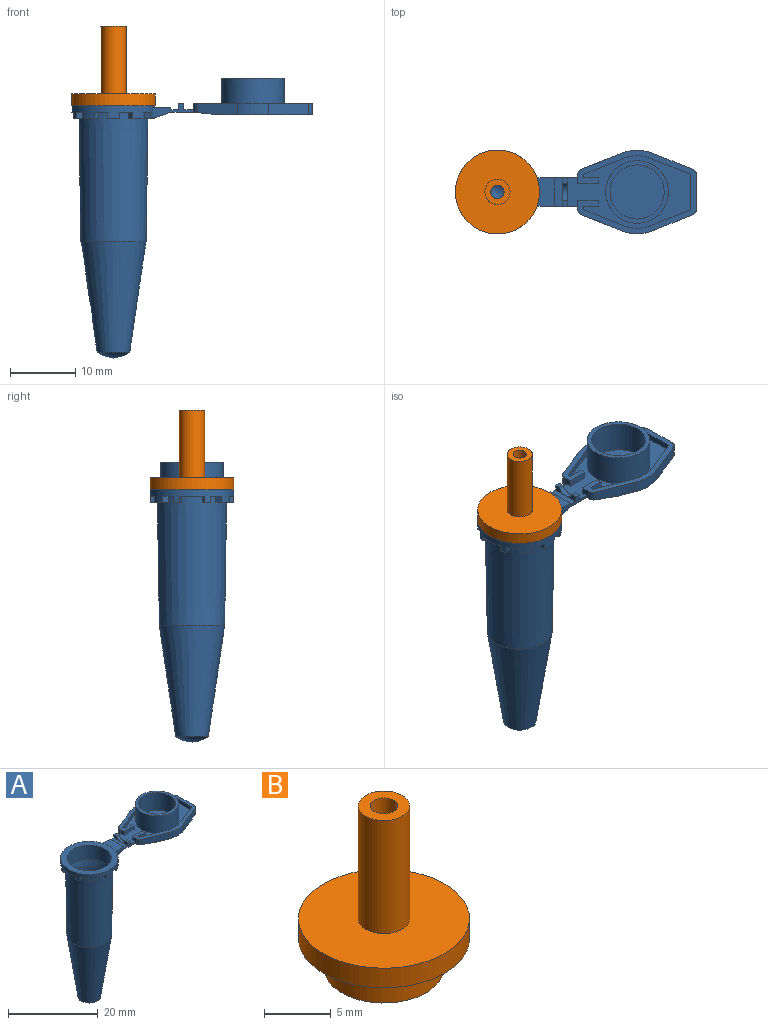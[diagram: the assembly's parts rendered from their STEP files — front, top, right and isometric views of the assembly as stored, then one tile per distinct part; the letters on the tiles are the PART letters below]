
ASSEMBLY  parts=2 mates=1
PART A: 116 faces, bbox 36.9x12.8x42.8 mm
  f0: plane 18.87x11.1mm, normal (0,0,1), area 74.1mm2, adj f1,f3,f65,f66,f75,f78,f93,f96
  f1: plane 1.4x1.25mm, normal (-1,0,0), area 1.4mm2, adj f0,f65,f87,f91,f114,f115
  f2: plane 0.82x0.78mm, normal (0,0,1), area 0.6mm2, adj f3,f65,f76,f77
  f3: plane 2.15x0.9mm, normal (1,0,0), area 1mm2, adj f0,f2,f65,f77
  f4: plane 2.15x0.9mm, normal (-1,0,0), area 1mm2, adj f66,f67,f74,f77
  f5: plane 7x4.3mm, normal (0,0,-1), area 23.5mm2, adj f17,f18,f51,f57,f65,f66,f70,f71
  f6: plane 1.96x1.52mm, normal (0,0,-1), area 1.9mm2, adj f17,f18,f27,f59
  f7: plane 2x1.85mm, normal (0,0,-1), area 1.9mm2, adj f17,f18,f55,f61
  f8: plane 2x1.85mm, normal (0,0,-1), area 1.9mm2, adj f17,f18,f47,f53
  f9: plane 1.96x1.52mm, normal (0,0,-1), area 1.9mm2, adj f17,f18,f43,f49
  f10: plane 1.96x1.52mm, normal (0,0,-1), area 1.9mm2, adj f17,f18,f39,f45
  f11: plane 2x1.85mm, normal (0,0,-1), area 1.9mm2, adj f17,f18,f36,f41
  f12: plane 3.8x1.32mm, normal (0,0,-1), area 3.8mm2, adj f17,f18,f63,f64
  f13: plane 2x1.85mm, normal (0,0,-1), area 1.9mm2, adj f17,f18,f29,f34
  f14: plane 1.96x1.52mm, normal (0,0,-1), area 1.9mm2, adj f17,f18,f25,f31
  f15: sphere r=4.1mm, area 21.9mm2, adj f19
  f16: plane 12.81x12.81mm, normal (0,0,1), area 52.5mm2, adj f17,f20
  f17: cylinder r=6.41mm len=12.81mm, axis (0,0,-1), area 52.2mm2, adj f5,f6,f7,f8,f9,f10,f11,f12
  f18: cone r=5.33mm half-angle=0.9deg, axis (0,0,1), area 643.6mm2, adj f5,f6,f7,f8,f9,f10,f11,f12
  f19: cone r=5mm half-angle=8.4deg, axis (0,0,1), area 403.7mm2, adj f15,f18
  f20: cylinder r=4.93mm len=9.86mm, axis (0,0,-1), area 117.7mm2, adj f16,f21
  f21: cone r=4.93mm half-angle=10.4deg, axis (0,0,1), area 54.8mm2, adj f20,f22
  f22: cone r=4.6mm half-angle=1.4deg, axis (0,0,1), area 406mm2, adj f21,f23
  f23: cone r=4.25mm half-angle=8.1deg, axis (0,0,1), area 315.3mm2, adj f22,f24
  f24: sphere r=2.02mm, area 22mm2, adj f23
  f25: plane 1.1x0.93mm, normal (-1,0,0), area 1mm2, adj f14,f17,f26,f28
  f26: cylinder r=5.33mm len=1.95mm, axis (0,0,1), area 1.8mm2, adj f18,f25,f27,f28
  f27: plane 1.1x0.93mm, normal (1,0,0), area 1mm2, adj f6,f17,f26,f28
  f28: plane 1.95x1.17mm, normal (0,0,-1), area 2.1mm2, adj f17,f25,f26,f27
  f29: plane 0.93x0.89mm, normal (-0.81,0.59,0), area 1mm2, adj f13,f17,f30,f32
  f30: cylinder r=5.33mm len=1.58mm, axis (0,0,1), area 1.8mm2, adj f18,f29,f31,f32
  f31: plane 0.93x0.89mm, normal (0.81,-0.59,0), area 1mm2, adj f14,f17,f30,f32
  f32: plane 2.22x2.03mm, normal (0,0,-1), area 2.1mm2, adj f17,f29,f30,f31
  f33: cylinder r=5.33mm len=0.98mm, axis (0,0,1), area 1mm2, adj f18,f34,f35,f64
  f34: plane 1.04x0.93mm, normal (0.31,-0.95,0), area 1mm2, adj f13,f17,f33,f35
  f35: plane 1.44x1.32mm, normal (0,0,-1), area 1.1mm2, adj f17,f33,f34,f64
  f36: plane 1.04x0.93mm, normal (0.31,0.95,0), area 1mm2, adj f11,f17,f37,f38
  f37: cylinder r=5.33mm len=0.98mm, axis (0,0,1), area 1mm2, adj f18,f36,f38,f63
  f38: plane 1.44x1.32mm, normal (0,0,-1), area 1.1mm2, adj f17,f36,f37,f63
  f39: plane 0.93x0.89mm, normal (0.81,0.59,0), area 1mm2, adj f10,f17,f40,f42
  f40: cylinder r=5.33mm len=1.58mm, axis (0,0,1), area 1.8mm2, adj f18,f39,f41,f42
  f41: plane 0.93x0.89mm, normal (-0.81,-0.59,0), area 1mm2, adj f11,f17,f40,f42
  f42: plane 2.22x2.03mm, normal (0,0,-1), area 2.1mm2, adj f17,f39,f40,f41
  f43: plane 1.1x0.93mm, normal (1,0,0), area 1mm2, adj f9,f17,f44,f46
  f44: cylinder r=5.33mm len=1.95mm, axis (0,0,1), area 1.8mm2, adj f18,f43,f45,f46
  f45: plane 1.1x0.93mm, normal (-1,0,0), area 1mm2, adj f10,f17,f44,f46
  f46: plane 1.95x1.17mm, normal (0,0,-1), area 2.1mm2, adj f17,f43,f44,f45
  f47: plane 0.93x0.89mm, normal (0.81,-0.59,0), area 1mm2, adj f8,f17,f48,f50
  f48: cylinder r=5.33mm len=1.58mm, axis (0,0,1), area 1.8mm2, adj f18,f47,f49,f50
  f49: plane 0.93x0.89mm, normal (-0.81,0.59,0), area 1mm2, adj f9,f17,f48,f50
  f50: plane 2.22x2.03mm, normal (0,0,-1), area 2.1mm2, adj f17,f47,f48,f49
  f51: plane 1.04x0.93mm, normal (0.31,-0.95,0), area 1mm2, adj f5,f17,f52,f54
  f52: cylinder r=5.33mm len=1.85mm, axis (0,0,1), area 1.8mm2, adj f18,f51,f53,f54
  f53: plane 1.04x0.93mm, normal (-0.31,0.95,0), area 1mm2, adj f8,f17,f52,f54
  f54: plane 2.19x1.64mm, normal (0,0,-1), area 2.1mm2, adj f17,f51,f52,f53
  f55: plane 1.04x0.93mm, normal (-0.31,-0.95,0), area 1mm2, adj f7,f17,f56,f58
  f56: cylinder r=5.33mm len=1.85mm, axis (0,0,1), area 1.8mm2, adj f18,f55,f57,f58
  f57: plane 1.04x0.93mm, normal (0.31,0.95,0), area 1mm2, adj f5,f17,f56,f58
  f58: plane 2.19x1.64mm, normal (0,0,-1), area 2.1mm2, adj f17,f55,f56,f57
  f59: plane 0.93x0.89mm, normal (-0.81,-0.59,0), area 1mm2, adj f6,f17,f60,f62
  f60: cylinder r=5.33mm len=1.58mm, axis (0,0,1), area 1.8mm2, adj f18,f59,f61,f62
  f61: plane 0.93x0.89mm, normal (0.81,0.59,0), area 1mm2, adj f7,f17,f60,f62
  f62: plane 2.22x2.03mm, normal (0,0,-1), area 2.1mm2, adj f17,f59,f60,f61
  f63: plane 1.03x0.93mm, normal (-0.31,-0.95,0), area 1mm2, adj f12,f17,f37,f38
  f64: plane 1.03x0.93mm, normal (-0.31,0.95,0), area 1mm2, adj f12,f17,f33,f35
  f65: plane 6.25x2.23mm, normal (0,-1,0), area 5.3mm2, adj f0,f1,f2,f3,f5,f17,f67,f68
  f66: plane 6.25x2.23mm, normal (0,1,0), area 5.3mm2, adj f0,f4,f5,f17,f67,f68,f69,f70
  f67: plane 4.3x1.16mm, normal (0,0,1), area 5mm2, adj f4,f65,f66,f69,f76
  f68: plane 4.3x2.75mm, normal (0,0,1), area 10.8mm2, adj f17,f65,f66,f69
  f69: plane 4.3x0.3mm, normal (1,0,0), area 1.3mm2, adj f65,f66,f67,f68
  f70: plane 2.76x0.93mm, normal (0.32,0,-0.95), area 2.2mm2, adj f5,f17,f66,f71
  f71: plane 2.52x0.85mm, normal (0,-1,0), area 1.1mm2, adj f5,f17,f70
  f72: plane 2.76x0.93mm, normal (0.32,0,-0.95), area 2.2mm2, adj f5,f17,f65,f73
  f73: plane 2.52x0.85mm, normal (0,1,0), area 1.1mm2, adj f5,f17,f72
  f74: plane 0.82x0.78mm, normal (0,0,1), area 0.6mm2, adj f4,f66,f75,f77
  f75: plane 2.15x0.9mm, normal (1,0,0), area 1mm2, adj f0,f66,f74,f77
  f76: plane 2.15x0.9mm, normal (-1,0,0), area 1mm2, adj f2,f65,f67,f77
  f77: cylinder r=1.5mm len=2.75mm, axis (1,0,0), area 2.9mm2, adj f2,f3,f4,f74,f75,f76
  f78: plane 1.4x1.25mm, normal (-1,0,0), area 1.4mm2, adj f0,f66,f87,f90,f96,f115
  f79: plane 6.09x2.44mm, normal (-0.37,0.93,0), area 11.2mm2, adj f80,f86,f87,f90,f115
  f80: cylinder r=6.4mm len=4.76mm, axis (0,0,1), area 8.8mm2, adj f79,f81,f86,f115
  f81: plane 6.09x2.44mm, normal (0.37,0.93,0), area 11.8mm2, adj f80,f86,f88,f115
  f82: plane 5.15x1.8mm, normal (1,0,0), area 9.3mm2, adj f86,f88,f89,f115
  f83: plane 6.09x2.44mm, normal (0.37,-0.93,0), area 11.8mm2, adj f84,f86,f89,f115
  f84: cylinder r=6.4mm len=4.76mm, axis (0,0,1), area 8.8mm2, adj f83,f85,f86,f115
  f85: plane 6.09x2.44mm, normal (-0.37,-0.93,0), area 11.2mm2, adj f84,f86,f87,f91,f115
  f86: plane 14.2x12.8mm, normal (0,0,-1), area 150.4mm2, adj f79,f80,f81,f82,f83,f84,f85,f87
  f87: plane 9.7x4mm, normal (-0.1,0,-1), area 32.4mm2, adj f1,f5,f78,f79,f85,f86,f90,f91
  f88: cylinder r=1mm len=1.8mm, axis (0,0,1), area 2.1mm2, adj f81,f82,f86,f115
  f89: cylinder r=1mm len=1.8mm, axis (0,0,1), area 2.1mm2, adj f82,f83,f86,f115
  f90: cylinder r=1mm len=1.46mm, axis (0,0,1), area 1.7mm2, adj f78,f79,f87,f115
  f91: cylinder r=1mm len=1.46mm, axis (0,0,1), area 1.7mm2, adj f1,f85,f87,f115
  f92: plane 9.6x9.6mm, normal (0,0,1), area 18.3mm2, adj f93,f94
  f93: cylinder r=4.8mm len=9.6mm, axis (0,0,-1), area 144.8mm2, adj f0,f92
  f94: cylinder r=4.15mm len=8.3mm, axis (0,0,-1), area 125.2mm2, adj f92,f95
  f95: plane 8.3x8.3mm, normal (0,0,1), area 54.1mm2, adj f94
  f96: plane 3.15x1mm, normal (0,-1,0), area 3.2mm2, adj f0,f78,f97,f115
  f97: plane 1x0.85mm, normal (1,0,0), area 0.9mm2, adj f0,f96,f98,f115
  f98: plane 2.3x1mm, normal (0,1,0), area 2.3mm2, adj f0,f97,f99,f115
  f99: plane 1x0.4mm, normal (1,0,0), area 0.4mm2, adj f0,f98,f100,f115
  f100: cylinder r=0.15mm len=1mm, axis (0,0,-1), area 0.2mm2, adj f0,f99,f101,f115
  f101: plane 6.09x2.44mm, normal (0.37,-0.93,0), area 6.6mm2, adj f0,f100,f102,f115
  f102: cylinder r=5.55mm len=4.13mm, axis (0,0,-1), area 4.2mm2, adj f0,f101,f103,f115
  f103: plane 6.09x2.44mm, normal (-0.37,-0.93,0), area 6.6mm2, adj f0,f102,f104,f115
  f104: cylinder r=0.15mm len=1mm, axis (0,0,-1), area 0.2mm2, adj f0,f103,f105,f115
  f105: plane 5.15x1mm, normal (-1,0,0), area 5.1mm2, adj f0,f104,f106,f115
  f106: cylinder r=0.15mm len=1mm, axis (0,0,-1), area 0.2mm2, adj f0,f105,f107,f115
  f107: plane 6.09x2.44mm, normal (-0.37,0.93,0), area 6.6mm2, adj f0,f106,f108,f115
  f108: cylinder r=5.55mm len=4.13mm, axis (0,0,-1), area 4.2mm2, adj f0,f107,f109,f115
  f109: plane 6.09x2.44mm, normal (0.37,0.93,0), area 6.6mm2, adj f0,f108,f110,f115
  f110: cylinder r=0.15mm len=1mm, axis (0,0,-1), area 0.2mm2, adj f0,f109,f111,f115
  f111: plane 1x0.4mm, normal (1,0,0), area 0.4mm2, adj f0,f110,f112,f115
  f112: plane 2.3x1mm, normal (0,-1,0), area 2.3mm2, adj f0,f111,f113,f115
  f113: plane 1x0.85mm, normal (1,0,0), area 0.9mm2, adj f0,f112,f114,f115
  f114: plane 3.15x1mm, normal (0,1,0), area 3.2mm2, adj f0,f1,f113,f115
  f115: plane 18.2x12.8mm, normal (0,0,1), area 42.8mm2, adj f1,f78,f79,f80,f81,f82,f83,f84
PART B: 8 faces, bbox 12.9x12.9x15 mm
  f0: plane 8.94x8.94mm, normal (0,0,-1), area 59.5mm2, adj f4,f7
  f1: plane 12.87x12.87mm, normal (0,0,1), area 118.3mm2, adj f2,f5
  f2: cylinder r=6.43mm len=12.87mm, axis (0,0,-1), area 73.2mm2, adj f1,f3
  f3: plane 12.87x12.87mm, normal (0,0,-1), area 67.3mm2, adj f2,f4
  f4: cylinder r=4.47mm len=8.94mm, axis (0,0,-1), area 78.4mm2, adj f0,f3
  f5: cylinder r=1.93mm len=10.4mm, axis (0,0,-1), area 126.1mm2, adj f1,f6
  f6: plane 3.86x3.86mm, normal (0,0,1), area 8.4mm2, adj f5,f7
  f7: cylinder r=1.03mm len=15mm, axis (0,0,-1), area 96.6mm2, adj f0,f6
PLACE A t=(0,0,-38.64)mm
PLACE B t=(0,0,-38.64)mm
MATE fastened B.f2 <-> A.f17  axis (0,0,-1) through (0,0,0)mm
